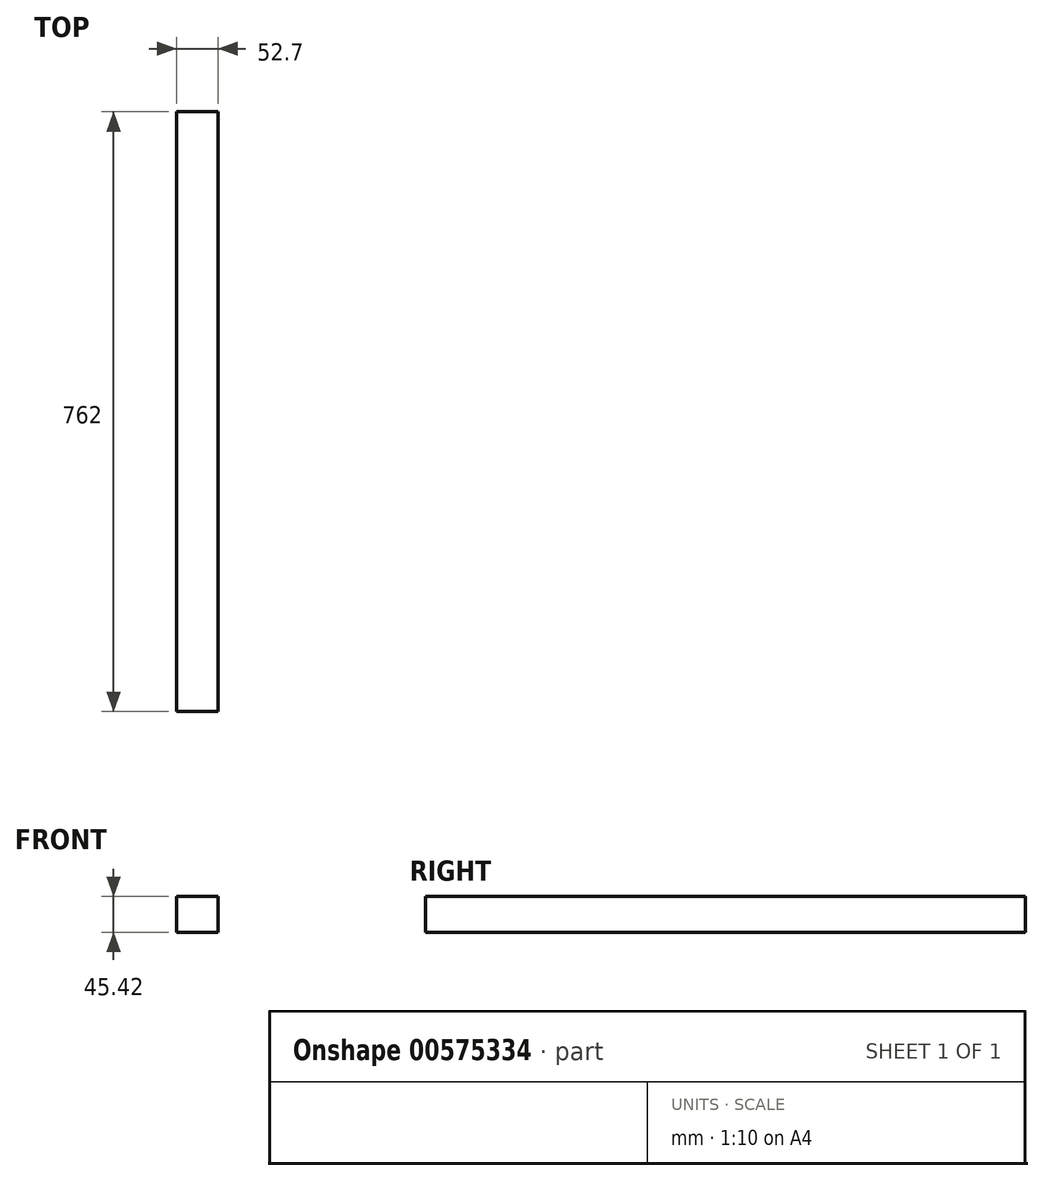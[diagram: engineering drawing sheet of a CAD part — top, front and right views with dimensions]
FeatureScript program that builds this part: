
annotation { "Feature Type Name" : "Feature", "Feature Type Description" : "" }
export const myFeature = defineFeature(function(context is Context, id is Id, definition is map)
    precondition{}
    {
        {
            var Q0;
            Q0=qCreatedBy(makeId("Front.planeOp"),FACE);
            var sketch = newSketch(context, id + "F0", { "sketchPlane" : qUnion([Q0])});
            skLineSegment(sketch, "E0", {"start": v(0, 0) * mm, "end": v(0, 45.42) * mm});
            skLineSegment(sketch, "E1", {"start": v(0, 45.42) * mm, "end": v(52.7, 45.42) * mm});
            skLineSegment(sketch, "E2", {"start": v(52.7, 45.42) * mm, "end": v(52.7, 0) * mm});
            skLineSegment(sketch, "E3", {"start": v(52.7, 0) * mm, "end": v(0, 0) * mm});
            skSolve(sketch);
        }
        {
            var Q0;
            Q0=makeQuery(id+"F0.imprint","IMPRINT",FACE,{"disambiguationData":[TD([[makeQuery(id+"F0.imprint","IMPRINT",EDGE,{"derivedFrom":sQuery(id+"F0.wireOp",EDGE,"E0")}),-1.0]])]});
            extrude(context, id + "F1", {"entities" : qUnion([Q0]), "depth" : 762 * mm, "offsetDistance" : 25.4 * mm});
        }
    });
